# Revit family: Hager-UNIVERS-Surface_mounted-IP30-Without_Cover-Without_DIN-Hosted-NL-en
name_source: partatom
category: Electrical Equipment
units: mm (PartAtom-declared; Revit-internal decimal feet)

## family parameters
Cut with Voids When Loaded = No
Host = Face
Maintain Annotation Orientation = Yes
Panel Configuration = Two Columns, Circuits Across
Part Type = Panelboard
Room Calculation Point = No
Round Connector Dimension = Use Diameter
Shared = No

## types (14) — shared parameters
BC_MODEL_ID = 1546901
BC_OBJECT_ID = 513402
BC_OBJECT_VERSION = #3
Code hager = ADD-EC000214_EU
EF000003 - Mounting method = Surface mounted
EF000007 - Colour = White
EF000024 - UV resistant = No
EF000049 - Depth = 160 mm  [stored 0.524934 ft]
EF000116 - RAL-number = 9010
EF000118 - With mounting plate = No
EF001062 - EMC-version = No
EF001088 - Extension possible = Yes
EF001134 - DIN-rail = No
EF004462 - Type of closure = Other
EF005474 - Degree of protection (IP) = IP30
EF006306 - With lock = No
EF015776 - Earthing terminal block = No
EF015777 - Neutral terminal block = No
EF015941 - Signal passing door = No
ETIM class code = EC000214
ETIM class name = Small distribution board
HG000002-With door or cover = No
HG000003-Range = UNIVERS
HG000005-Thickness = 2 mm  [stored 0.00656168 ft]
HG000006-Flush mounted = No
HG000011-Empty rows from bottom = No
HG000012-Door swing angle = 90.00°
HG000013-Door on the left = No
HG000014-Door on the right = Yes
HG000015-Clearance visibility = Yes
HG000016-Door 3D visibility = Yes
HG000017-Distance between poles = 18 mm  [stored 0.0590551 ft]
HG000060-RAL-number = 9010
HG000099-Onfly Template ID = 507532
Manufacturer = Hager
Name = UNIVERS-Surface_mounted-IP30-Without_Cover-Without_DIN-NL
Name BIM&CO = Electricity
Name hager = ADD_Enclosures_EC000214
Uniformat = Low Tension Service & Dist.
Uniformat code = D501001
zero-valued in all types: Default Elevation, EF001131 - Inner depth, HG000007-Number of empty columns, HG000008-Number of empty rows

## per-type parameters (varying)
| type | BC_VARIANT_ID | EF000008 - Width | EF000040 - Height | EF000218 - Built-in depth | EF000266 - Number of rows | EF000332 - Built-in height | EF000846 - Built-in width | EF002950 - Width in number of modular spacings | EF006244 - Transparent cover/door | EF009212 - Cover model | HG000001-Number of columns | HG000004-Manufacturer reference | HG000009-Double swing door | HG000010-Asymmetric doors | HGEF000266-Number of rows | HGEF002950-Width in number of modular spacings |
| UNIVERS-Surface_mounted_W300_H500_D160_12_Modular_Spacing-FWQ31P1 | 1173236 | 300 mm | 500 mm  [stored 1.64042 ft] | 0 mm  [stored 0 ft] | 3 | 500 mm  [stored 1.64042 ft] | 300 mm | 12 | No | Closed | 1 | FWQ31P1 | No | No | 3 | 12 |
| UNIVERS-Surface_mounted_W1050_H500_D160_48_Modular_Spacing-FWQ34P1 | 1173237 | 1050 mm | 500 mm  [stored 1.64042 ft] | 0 mm  [stored 0 ft] | 3 | 500 mm  [stored 1.64042 ft] | 1050 mm | 48 | No | With notch | 4 | FWQ34P1 | Yes | No | 3 | 48 |
| UNIVERS-Surface_mounted_W300_H650_D160_12_Modular_Spacing-FWQ41P1 | 1173238 | 300 mm | 650 mm  [stored 2.13255 ft] | 0 mm  [stored 0 ft] | 4 | 650 mm  [stored 2.13255 ft] | 300 mm | 12 | No | With notch | 1 | FWQ41P1 | No | No | 4 | 12 |
| UNIVERS-Surface_mounted_W1050_H650_D160_48_Modular_Spacing-FWQ44P1 | 1173239 | 1050 mm | 650 mm  [stored 2.13255 ft] | 0 mm  [stored 0 ft] | 4 | 650 mm  [stored 2.13255 ft] | 1050 mm | 48 | No | With notch | 4 | FWQ44P1 | Yes | No | 4 | 48 |
| UNIVERS-Surface_mounted_W300_H800_D160_12_Modular_Spacing-FWQ51P1 | 1173240 | 300 mm | 800 mm  [stored 2.62467 ft] | 0 mm  [stored 0 ft] | 5 | 800 mm  [stored 2.62467 ft] | 300 mm | 12 | Yes | With notch | 1 | FWQ51P1 | No | No | 5 | 12 |
| UNIVERS-Surface_mounted_W1050_H800_D160_12_Modular_Spacing-FWQ54P1 | 1173241 | 1050 mm | 800 mm  [stored 2.62467 ft] | 0 mm  [stored 0 ft] | 5 | 800 mm  [stored 2.62467 ft] | 1050 mm | 12 | Yes | With notch | 4 | FWQ54P1 | Yes | No | 5 | 12 |
| UNIVERS-Surface_mounted_W300_H950_D160_12_Modular_Spacing-FWQ61P1 | 1173242 | 300 mm | 950 mm  [stored 3.1168 ft] | 0 mm  [stored 0 ft] | 6 | 950 mm  [stored 3.1168 ft] | 300 mm | 12 | No | With notch | 1 | FWQ61P1 | No | No | 6 | 12 |
| UNIVERS-Surface_mounted_W550_H950_D160_24_Modular_Spacing-FWQ62P1 | 1173243 | 550 mm | 950 mm  [stored 3.1168 ft] | 0 mm  [stored 0 ft] | 6 | 950 mm  [stored 3.1168 ft] | 550 mm | 24 | No | With notch | 2 | FWQ62P1 | No | No | 6 | 24 |
| UNIVERS-Surface_mounted_W800_H950_D160_36_Modular_Spacing-FWQ63P1 | 1173244 | 800 mm  [stored 2.62467 ft] | 950 mm  [stored 3.1168 ft] | 0 mm  [stored 0 ft] | 6 | 950 mm  [stored 3.1168 ft] | 800 mm  [stored 2.62467 ft] | 36 | No | With notch | 3 | FWQ63P1 | Yes | Yes | 6 | 36 |
| UNIVERS-Surface_mounted_W1050_H950_D160_48_Modular_Spacing-FWQ64P1 | 1173245 | 1050 mm | 950 mm  [stored 3.1168 ft] | 0 mm  [stored 0 ft] | 6 | 950 mm  [stored 3.1168 ft] | 1050 mm | 48 | Yes | With notch | 4 | FWQ64P1 | Yes | No | 6 | 48 |
| UNIVERS-Surface_mounted_W300_H1100_D160_12_Modular_Spacing-FWQ71P1 | 1173246 | 300 mm | 1100 mm  [stored 3.60892 ft] | 0 mm  [stored 0 ft] | 7 | 1100 mm  [stored 3.60892 ft] | 300 mm | 12 | No | With notch | 1 | FWQ71P1 | No | No | 7 | 12 |
| UNIVERS-Surface_mounted_W550_H1100_D160_12_Modular_Spacing-FWQ72P1 | 1173247 | 550 mm | 1100 mm  [stored 3.60892 ft] | 0 mm  [stored 0 ft] | 7 | 1100 mm  [stored 3.60892 ft] | 550 mm | 12 | No | With notch | 2 | FWQ72P1 | No | No | 7 | 12 |
| UNIVERS-Surface_mounted_W800_H1100_D160_12_Modular_Spacing-FWQ73P1 | 1173248 | 800 mm  [stored 2.62467 ft] | 1100 mm  [stored 3.60892 ft] | 0 mm  [stored 0 ft] | 7 | 1100 mm  [stored 3.60892 ft] | 800 mm  [stored 2.62467 ft] | 12 | Yes | With notch | 3 | FWQ73P1 | Yes | Yes | 7 | 12 |
| UNIVERS-Surface_mounted_W1050_H1100_D160_12_Modular_Spacing-FWQ74P1 | 1173249 | 1050 mm | 1100 mm  [stored 3.60892 ft] | 161 mm  [stored 0.528215 ft] | 7 | 1100 mm  [stored 3.60892 ft] | 1050 mm | 12 | No | With notch | 4 | FWQ74P1 | Yes | No | 7 | 12 |

note: column(s) folded — value = type name in every type: Reference

note: [stored X ft] marks values corroborated as IEEE doubles in the binary element streams (Revit-internal decimal feet)

## geometry (parser evidence)
native form markers: Sweep x16
no freeform markers — native parametric forms only
